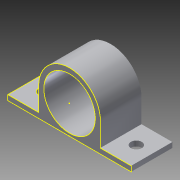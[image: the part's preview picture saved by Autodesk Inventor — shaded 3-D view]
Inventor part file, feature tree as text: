
AUTODESK INVENTOR PART (.ipt)
format: ipt  version: 2013 (Build 170138000, 138)  size: 143,360 bytes
history: native  units: in
note: dims shown in document units (in); Inventor stores cm internally (conversion verified against a paired STEP export)
features: sketch x4, extrude x2
ambient origin geometry x8: Origin, YZ Plane, XZ Plane, XY Plane, X Axis, Y Axis, Z Axis, Center Point
bodies: Solid1 (feature_tree)
feature tree (6):
  extrude  "Extrusion1"  Depth=1.5in
  extrude  "Extrusion2"  Depth=0.6875in
  sketch  "Sketch3"  dims[d4=1.25in]
  sketch  "Sketch4"  dims[d5=0.125in d6=1.0in d7=0.0in d8=0.266in d11=1.0in d12=0.0in d13=0.375in d14=0.266in d15=0.375in]
  sketch  "Sketch1"  dims[d0=1.5in d1=1.5in]
  sketch  "Sketch2"  dims[d2=0.125in d3=0.6875in]
